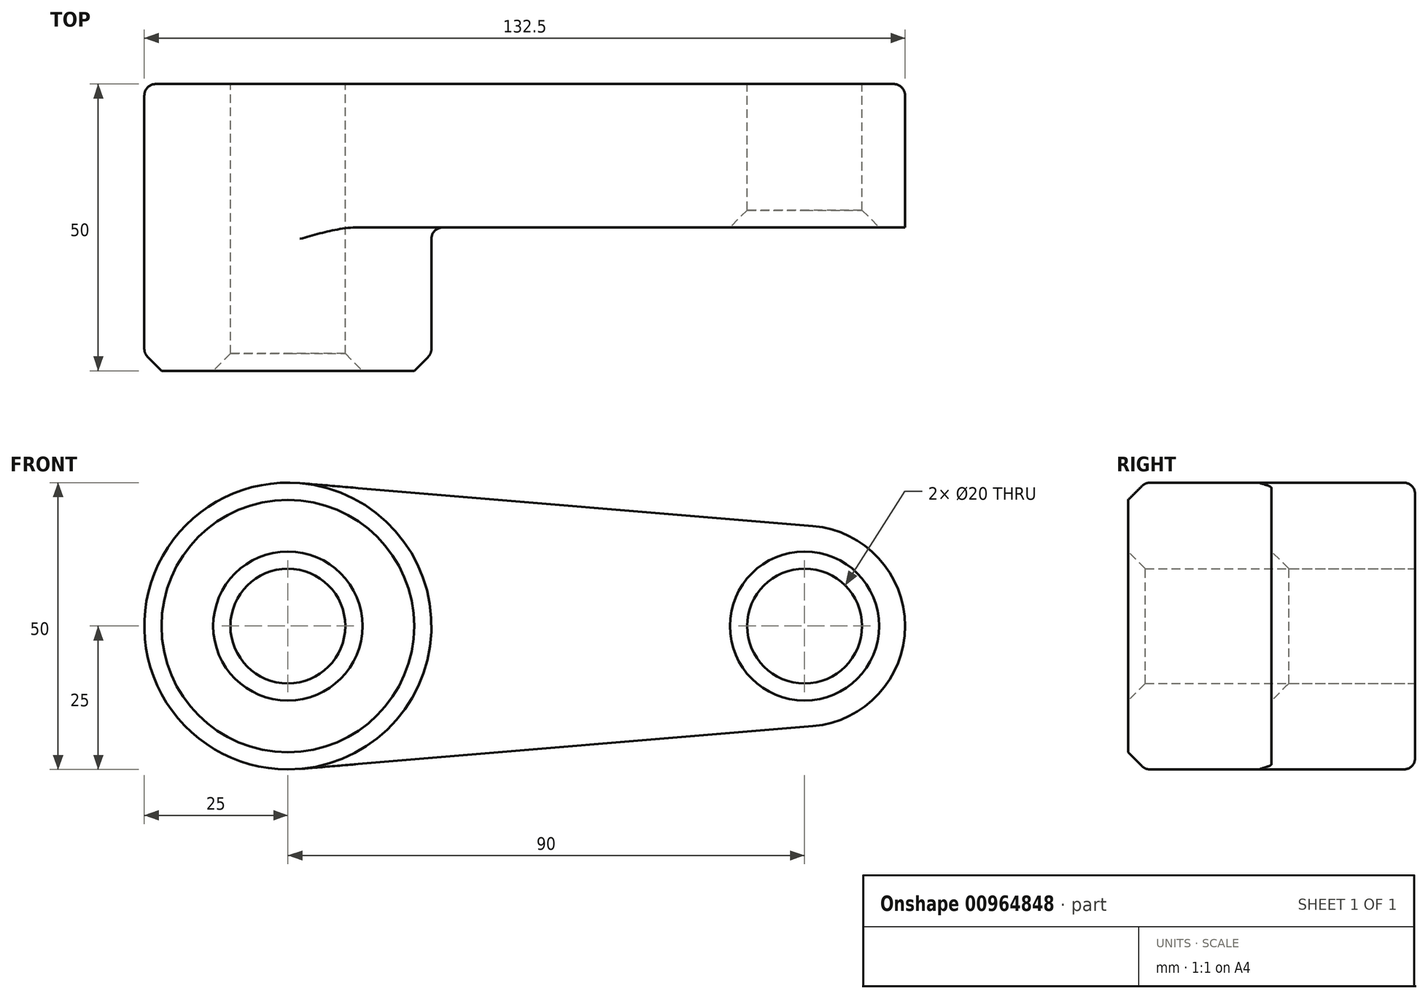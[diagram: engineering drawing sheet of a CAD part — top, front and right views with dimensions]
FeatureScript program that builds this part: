
annotation { "Feature Type Name" : "Feature", "Feature Type Description" : "" }
export const myFeature = defineFeature(function(context is Context, id is Id, definition is map)
    precondition{}
    {
        {
            var Q0;
            Q0=qCreatedBy(makeId("Front.planeOp"),FACE);
            var sketch = newSketch(context, id + "F0", { "sketchPlane" : qUnion([Q0])});
            skCircle(sketch, "E0", {"center": v(0, 0) * mm, "radius": 25 * mm});
            skCircle(sketch, "E1", {"center": v(90, 0) * mm, "radius": 17.5 * mm});
            skLineSegment(sketch, "E2", {"start": v(2.08, 24.91) * mm, "end": v(91.46, 17.44) * mm});
            skLineSegment(sketch, "E3", {"start": v(2.08, -24.91) * mm, "end": v(91.46, -17.44) * mm});
            skCircle(sketch, "E4", {"center": v(0, 0) * mm, "radius": 10 * mm});
            skCircle(sketch, "E5", {"center": v(90, 0) * mm, "radius": 10 * mm});
            skSolve(sketch);
        }
        {
            var Q0;
            Q0=qSketchRegion(id+"F0",true);
            extrude(context, id + "F1", {"entities" : qUnion([Q0]), "depth" : 25 * mm});
        }
        {
            var Q0;
            Q0=makeQuery(id+"F0.imprint","IMPRINT",FACE,{"disambiguationData":[TD([[makeQuery(id+"F0.imprint","IMPRINT",EDGE,{"derivedFrom":sQuery(id+"F0.wireOp",EDGE,"E4")}),-1.0]])]});
            extrude(context, id + "F2", {"entities" : qUnion([Q0]), "operationType" : NewBodyOperationType.ADD, "depth" : 50 * mm});
        }
        {
            var Q0;
            Q0=makeQuery(id+"F2.opExtrude","CAP_EDGE",EDGE,{"disambiguationData":[OSD([sQuery(id+"F0.wireOp",EDGE,"E0")])],"isStart":false});
            var Q1;
            Q1=makeQuery(id+"F2.opExtrude","CAP_EDGE",EDGE,{"disambiguationData":[OSD([sQuery(id+"F0.wireOp",EDGE,"E4")])],"isStart":false});
            var Q2;
            Q2=makeQuery(id+"F1.opExtrude","CAP_EDGE",EDGE,{"disambiguationData":[OSD([sQuery(id+"F0.wireOp",EDGE,"E5")])],"isStart":false});
            chamfer(context, id + "F3", {"entities" : qUnion([Q0, Q1, Q2]), "width" : 3 * mm, "tangentPropagation" : true});
        }
        {
            var Q0;
            {var subQ0=sQuery(id+"F0.wireOp",EDGE,"E0");Q0=makeQuery(id+"F2.boolean.opBoolean","MERGE",FACE,{"derivedFrom":[makeQuery(id+"F1.opExtrude","SWEPT_FACE",FACE,{"disambiguationData":[OSD([subQ0])]}),makeQuery(id+"F2.opExtrude","SWEPT_FACE",FACE,{"disambiguationData":[OSD([subQ0])]})]});}
            fillet(context, id + "F4", {"entities" : qUnion([Q0]), "radius" : 2 * mm, "tangentPropagation" : true, "allowEdgeOverflow" : false});
        }
    });
